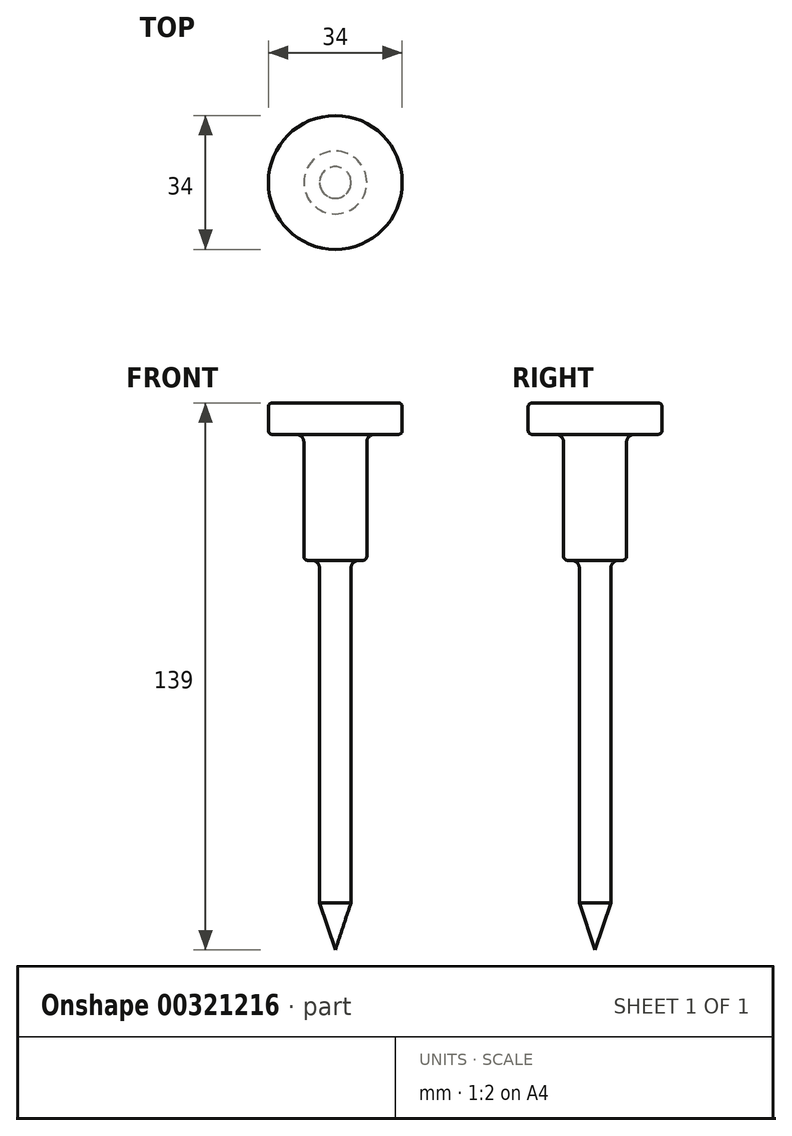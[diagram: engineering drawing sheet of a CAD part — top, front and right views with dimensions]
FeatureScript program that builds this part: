
annotation { "Feature Type Name" : "Feature", "Feature Type Description" : "" }
export const myFeature = defineFeature(function(context is Context, id is Id, definition is map)
    precondition{}
    {
        {
            var Q0;
            Q0=qCreatedBy(makeId("Front.planeOp"),FACE);
            var sketch = newSketch(context, id + "F0", { "sketchPlane" : qUnion([Q0])});
            skLineSegment(sketch, "E0", {"start": v(0, 69.5) * mm, "end": v(0, -69.5) * mm});
            skLineSegment(sketch, "E1", {"start": v(0, 69.5) * mm, "end": v(17, 69.5) * mm});
            skLineSegment(sketch, "E2", {"start": v(17, 69.5) * mm, "end": v(17, 61.5) * mm});
            skLineSegment(sketch, "E3", {"start": v(17, 61.5) * mm, "end": v(8, 61.5) * mm});
            skLineSegment(sketch, "E4", {"start": v(8, 61.5) * mm, "end": v(8, 39.5) * mm});
            skLineSegment(sketch, "E5", {"start": v(8, 39.5) * mm, "end": v(8, 29.5) * mm});
            skLineSegment(sketch, "E6", {"start": v(8, 29.5) * mm, "end": v(4, 29.5) * mm});
            skLineSegment(sketch, "E7", {"start": v(4, 29.5) * mm, "end": v(4, -57.5) * mm});
            skLineSegment(sketch, "E8", {"start": v(4, -57.5) * mm, "end": v(0, -69.5) * mm});
            skSolve(sketch);
        }
        {
            var Q0;
            Q0=makeQuery(id+"F0.imprint","IMPRINT",FACE,{"disambiguationData":[TD([[makeQuery(id+"F0.imprint","IMPRINT",EDGE,{"derivedFrom":sQuery(id+"F0.wireOp",EDGE,"E0")}),1.0]])]});
            var Q1;
            Q1=sQuery(id+"F0.wireOp",EDGE,"E0");
            revolve(context, id + "F1", {"entities" : qUnion([Q0]), "axis" : qUnion([Q1]), "revolveType" : RevolveType.FULL});
        }
        {
            var Q0;
            Q0=makeQuery(id+"F1.opRevolve","SWEPT_EDGE",EDGE,{"disambiguationData":[OSD([sQuery(id+"F0.wireOp",EDGE,"E1"),sQuery(id+"F0.wireOp",EDGE,"E2")])]});
            var Q1;
            Q1=makeQuery(id+"F1.opRevolve","SWEPT_EDGE",EDGE,{"disambiguationData":[OSD([sQuery(id+"F0.wireOp",EDGE,"E2"),sQuery(id+"F0.wireOp",EDGE,"E3")])]});
            var Q2;
            Q2=makeQuery(id+"F1.opRevolve","SWEPT_EDGE",EDGE,{"disambiguationData":[OSD([sQuery(id+"F0.wireOp",EDGE,"E5"),sQuery(id+"F0.wireOp",EDGE,"E6")])]});
            fillet(context, id + "F2", {"entities" : qUnion([Q0, Q1, Q2]), "radius" : 1 * mm, "tangentPropagation" : true, "allowEdgeOverflow" : false});
        }
        {
            var Q0;
            Q0=makeQuery(id+"F1.opRevolve","SWEPT_EDGE",EDGE,{"disambiguationData":[OSD([sQuery(id+"F0.wireOp",EDGE,"E3"),sQuery(id+"F0.wireOp",EDGE,"E4")])]});
            var Q1;
            Q1=makeQuery(id+"F1.opRevolve","SWEPT_EDGE",EDGE,{"disambiguationData":[OSD([sQuery(id+"F0.wireOp",EDGE,"E6"),sQuery(id+"F0.wireOp",EDGE,"E7")])]});
            fillet(context, id + "F3", {"entities" : qUnion([Q0, Q1]), "radius" : 2 * mm, "tangentPropagation" : true, "allowEdgeOverflow" : false});
        }
    });
